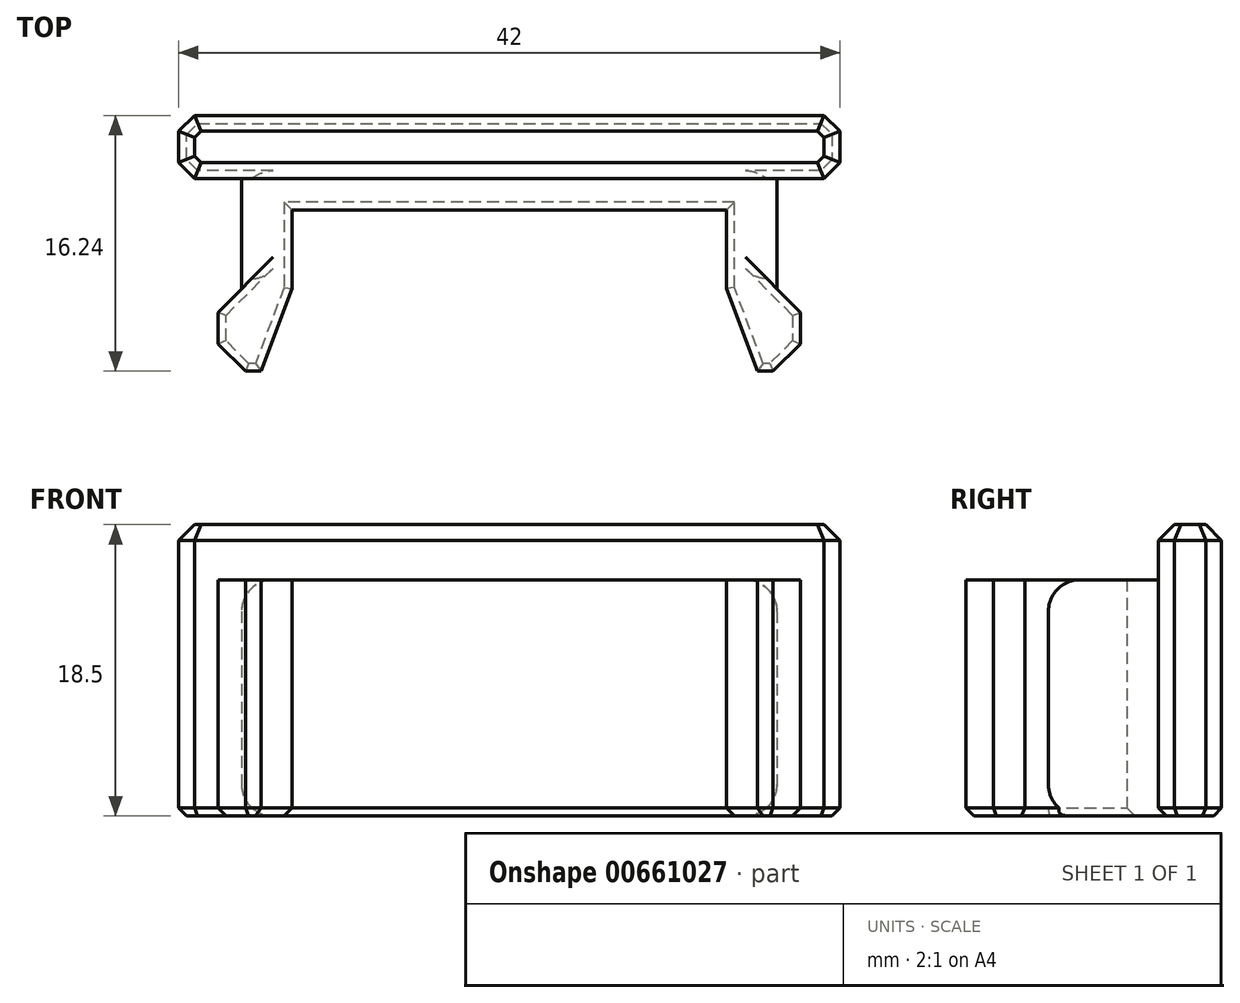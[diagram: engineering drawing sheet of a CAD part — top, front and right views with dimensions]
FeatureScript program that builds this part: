
annotation { "Feature Type Name" : "Feature", "Feature Type Description" : "" }
export const myFeature = defineFeature(function(context is Context, id is Id, definition is map)
    precondition{}
    {
        {
            var Q0;
            Q0=qCreatedBy(makeId("Top.planeOp"),FACE);
            var sketch = newSketch(context, id + "F0", { "sketchPlane" : qUnion([Q0])});
            skLineSegment(sketch, "E0.bottom", {"start": v(-20, 0) * mm, "end": v(-17.5, 0) * mm});
            skLineSegment(sketch, "E0.top", {"start": v(-20, -10) * mm, "end": v(-17.5, -10) * mm});
            skLineSegment(sketch, "E0.left", {"start": v(-20, 0) * mm, "end": v(-20, -10) * mm});
            skLineSegment(sketch, "E0.right", {"start": v(-17.5, 0) * mm, "end": v(-17.5, -10) * mm});
            skLineSegment(sketch, "E1.bottom", {"start": v(17.5, 0) * mm, "end": v(20, 0) * mm});
            skLineSegment(sketch, "E1.top", {"start": v(17.5, -10) * mm, "end": v(20, -10) * mm});
            skLineSegment(sketch, "E1.left", {"start": v(17.5, 0) * mm, "end": v(17.5, -10) * mm});
            skLineSegment(sketch, "E1.right", {"start": v(20, 0) * mm, "end": v(20, -10) * mm});
            skLineSegment(sketch, "E2", {"start": v(-20, 0) * mm, "end": v(-21, 1) * mm});
            skLineSegment(sketch, "E3", {"start": v(-21, 1) * mm, "end": v(-21, 3) * mm});
            skLineSegment(sketch, "E4", {"start": v(-21, 3) * mm, "end": v(-20, 4) * mm});
            skLineSegment(sketch, "E5", {"start": v(-20, 4) * mm, "end": v(0, 4) * mm});
            skLineSegment(sketch, "E6", {"start": v(-17.5, 0) * mm, "end": v(-17, 0) * mm});
            skLineSegment(sketch, "E7", {"start": v(-17, 0) * mm, "end": v(-17, -7) * mm});
            skLineSegment(sketch, "E8", {"start": v(-17, -7) * mm, "end": v(-18.5, -8.5) * mm});
            skLineSegment(sketch, "E9", {"start": v(-18.5, -8.5) * mm, "end": v(-18.5, -10.5) * mm});
            skLineSegment(sketch, "E10", {"start": v(-18.5, -10.5) * mm, "end": v(-16.76, -12.24) * mm});
            skLineSegment(sketch, "E11", {"start": v(-16.76, -12.24) * mm, "end": v(-15.76, -12.24) * mm});
            skLineSegment(sketch, "E12", {"start": v(-15.76, -12.24) * mm, "end": v(-13.8, -7) * mm});
            skLineSegment(sketch, "E13", {"start": v(-13.8, -7) * mm, "end": v(-13.8, -2) * mm});
            skLineSegment(sketch, "E14", {"start": v(-13.8, -2) * mm, "end": v(0, -2) * mm});
            skLineSegment(sketch, "E15.MirrorCS", {"start": v(20, 4) * mm, "end": v(0, 4) * mm});
            skLineSegment(sketch, "E16.MirrorCS", {"start": v(21, 3) * mm, "end": v(20, 4) * mm});
            skLineSegment(sketch, "E17.MirrorCS", {"start": v(21, 1) * mm, "end": v(21, 3) * mm});
            skLineSegment(sketch, "E18.MirrorCS", {"start": v(20, 0) * mm, "end": v(21, 1) * mm});
            skLineSegment(sketch, "E19.MirrorCS", {"start": v(17.5, 0) * mm, "end": v(17, 0) * mm});
            skLineSegment(sketch, "E20.MirrorCS", {"start": v(17, 0) * mm, "end": v(17, -7) * mm});
            skLineSegment(sketch, "E21.MirrorCS", {"start": v(17, -7) * mm, "end": v(18.5, -8.5) * mm});
            skLineSegment(sketch, "E22.MirrorCS", {"start": v(18.5, -8.5) * mm, "end": v(18.5, -10.5) * mm});
            skLineSegment(sketch, "E23.MirrorCS", {"start": v(18.5, -10.5) * mm, "end": v(16.76, -12.24) * mm});
            skLineSegment(sketch, "E24.MirrorCS", {"start": v(16.76, -12.24) * mm, "end": v(15.76, -12.24) * mm});
            skLineSegment(sketch, "E25.MirrorCS", {"start": v(15.76, -12.24) * mm, "end": v(13.8, -7) * mm});
            skLineSegment(sketch, "E26.MirrorCS", {"start": v(13.8, -7) * mm, "end": v(13.8, -2) * mm});
            skLineSegment(sketch, "E27.MirrorCS", {"start": v(13.8, -2) * mm, "end": v(0, -2) * mm});
            skSolve(sketch);
        }
        {
            var Q0;
            Q0=makeQuery(id+"F0.imprint","IMPRINT",FACE,{"disambiguationData":[TD([[makeQuery(id+"F0.imprint","IMPRINT",EDGE,{"derivedFrom":sQuery(id+"F0.wireOp",EDGE,"E0.bottom")}),1.0]])]});
            var Q1;
            {var subQ0=sQuery(id+"F0.wireOp",EDGE,"E0.right");var subQ1=sQuery(id+"F0.wireOp",EDGE,"E0.top");var subQ2=makeQuery(id+"F0.imprint","INTERSECT",VERTEX,{"derivedFrom":[subQ1,subQ0]});Q1=makeQuery(id+"F0.imprint","IMPRINT",FACE,{"disambiguationData":[TD([[makeQuery(id+"F0.imprint","IMPRINT",EDGE,{"disambiguationData":[TD([[subQ2,1.0]])],"derivedFrom":subQ1}),1.0]])]});}
            var Q2;
            {var subQ0=sQuery(id+"F0.wireOp",EDGE,"E1.left");var subQ1=sQuery(id+"F0.wireOp",EDGE,"E1.top");var subQ2=makeQuery(id+"F0.imprint","INTERSECT",VERTEX,{"derivedFrom":[subQ1,subQ0]});Q2=makeQuery(id+"F0.imprint","IMPRINT",FACE,{"disambiguationData":[TD([[makeQuery(id+"F0.imprint","IMPRINT",EDGE,{"disambiguationData":[TD([[subQ2,-1.0]])],"derivedFrom":subQ1}),1.0]])]});}
            extrude(context, id + "F1", {"entities" : qUnion([Q0, Q1, Q2]), "depth" : 15 * mm, "offsetDistance" : 25 * mm});
        }
        {
            var Q0;
            Q0=makeQuery(id+"F1.opExtrude","CAP_FACE",FACE,{"disambiguationData":[OSD([sQuery(id+"F0.wireOp",EDGE,"E0.bottom"),sQuery(id+"F0.wireOp",EDGE,"E1.bottom"),sQuery(id+"F0.wireOp",EDGE,"E2"),sQuery(id+"F0.wireOp",EDGE,"E3"),sQuery(id+"F0.wireOp",EDGE,"E4"),sQuery(id+"F0.wireOp",EDGE,"E5"),sQuery(id+"F0.wireOp",EDGE,"E6"),sQuery(id+"F0.wireOp",EDGE,"E7"),sQuery(id+"F0.wireOp",EDGE,"E8"),sQuery(id+"F0.wireOp",EDGE,"E9"),sQuery(id+"F0.wireOp",EDGE,"E10"),sQuery(id+"F0.wireOp",EDGE,"E11"),sQuery(id+"F0.wireOp",EDGE,"E12"),sQuery(id+"F0.wireOp",EDGE,"E13"),sQuery(id+"F0.wireOp",EDGE,"E14"),sQuery(id+"F0.wireOp",EDGE,"E15.MirrorCS"),sQuery(id+"F0.wireOp",EDGE,"E16.MirrorCS"),sQuery(id+"F0.wireOp",EDGE,"E17.MirrorCS"),sQuery(id+"F0.wireOp",EDGE,"E18.MirrorCS"),sQuery(id+"F0.wireOp",EDGE,"E19.MirrorCS"),sQuery(id+"F0.wireOp",EDGE,"E20.MirrorCS"),sQuery(id+"F0.wireOp",EDGE,"E21.MirrorCS"),sQuery(id+"F0.wireOp",EDGE,"E22.MirrorCS"),sQuery(id+"F0.wireOp",EDGE,"E23.MirrorCS"),sQuery(id+"F0.wireOp",EDGE,"E24.MirrorCS"),sQuery(id+"F0.wireOp",EDGE,"E25.MirrorCS"),sQuery(id+"F0.wireOp",EDGE,"E26.MirrorCS"),sQuery(id+"F0.wireOp",EDGE,"E27.MirrorCS")])],"isStart":false});
            var sketch = newSketch(context, id + "F2", { "sketchPlane" : qUnion([Q0])});
            skLineSegment(sketch, "E28", {"start": v(-17, 0) * mm, "end": v(17, 0) * mm});
            skSolve(sketch);
        }
        {
            var Q0;
            Q0=makeQuery(id+"F2.imprint","IMPRINT",FACE,{"disambiguationData":[TD([[makeQuery(id+"F2.imprint","IMPRINT",EDGE,{"derivedFrom":sQuery(id+"F2.wireOp",EDGE,"E28")}),1.0]])]});
            extrude(context, id + "F3", {"entities" : qUnion([Q0]), "operationType" : NewBodyOperationType.ADD, "depth" : 3.5 * mm, "offsetDistance" : 25 * mm});
        }
        {
            var Q0;
            Q0=makeQuery(id+"F3.opExtrude","CAP_FACE",FACE,{"disambiguationData":[OSD([sQuery(id+"F0.wireOp",EDGE,"E0.bottom"),sQuery(id+"F0.wireOp",EDGE,"E1.bottom"),sQuery(id+"F0.wireOp",EDGE,"E2"),sQuery(id+"F0.wireOp",EDGE,"E3"),sQuery(id+"F0.wireOp",EDGE,"E4"),sQuery(id+"F0.wireOp",EDGE,"E5"),sQuery(id+"F0.wireOp",EDGE,"E6"),sQuery(id+"F0.wireOp",EDGE,"E15.MirrorCS"),sQuery(id+"F0.wireOp",EDGE,"E16.MirrorCS"),sQuery(id+"F0.wireOp",EDGE,"E17.MirrorCS"),sQuery(id+"F0.wireOp",EDGE,"E18.MirrorCS"),sQuery(id+"F0.wireOp",EDGE,"E19.MirrorCS"),sQuery(id+"F2.wireOp",EDGE,"E28")])],"isStart":false});
            chamfer(context, id + "F4", {"entities" : qUnion([Q0]), "width" : 1 * mm, "tangentPropagation" : true});
        }
        {
            var Q0;
            Q0=makeQuery(id+"F1.opExtrude","CAP_EDGE",EDGE,{"disambiguationData":[OSD([sQuery(id+"F0.wireOp",EDGE,"E7")])],"isStart":true});
            var Q1;
            Q1=makeQuery(id+"F1.opExtrude","CAP_EDGE",EDGE,{"disambiguationData":[OSD([sQuery(id+"F0.wireOp",EDGE,"E7")])],"isStart":false});
            var Q2;
            Q2=makeQuery(id+"F1.opExtrude","CAP_EDGE",EDGE,{"disambiguationData":[OSD([sQuery(id+"F0.wireOp",EDGE,"E20.MirrorCS")])],"isStart":true});
            var Q3;
            Q3=makeQuery(id+"F1.opExtrude","CAP_EDGE",EDGE,{"disambiguationData":[OSD([sQuery(id+"F0.wireOp",EDGE,"E20.MirrorCS")])],"isStart":false});
            fillet(context, id + "F5", {"entities" : qUnion([Q0, Q1, Q2, Q3]), "radius" : 2 * mm, "tangentPropagation" : true, "allowEdgeOverflow" : false});
        }
        {
            var Q0;
            Q0=makeQuery(id+"F1.opExtrude","CAP_FACE",FACE,{"disambiguationData":[OSD([sQuery(id+"F0.wireOp",EDGE,"E0.bottom"),sQuery(id+"F0.wireOp",EDGE,"E1.bottom"),sQuery(id+"F0.wireOp",EDGE,"E2"),sQuery(id+"F0.wireOp",EDGE,"E3"),sQuery(id+"F0.wireOp",EDGE,"E4"),sQuery(id+"F0.wireOp",EDGE,"E5"),sQuery(id+"F0.wireOp",EDGE,"E6"),sQuery(id+"F0.wireOp",EDGE,"E7"),sQuery(id+"F0.wireOp",EDGE,"E8"),sQuery(id+"F0.wireOp",EDGE,"E9"),sQuery(id+"F0.wireOp",EDGE,"E10"),sQuery(id+"F0.wireOp",EDGE,"E11"),sQuery(id+"F0.wireOp",EDGE,"E12"),sQuery(id+"F0.wireOp",EDGE,"E13"),sQuery(id+"F0.wireOp",EDGE,"E14"),sQuery(id+"F0.wireOp",EDGE,"E15.MirrorCS"),sQuery(id+"F0.wireOp",EDGE,"E16.MirrorCS"),sQuery(id+"F0.wireOp",EDGE,"E17.MirrorCS"),sQuery(id+"F0.wireOp",EDGE,"E18.MirrorCS"),sQuery(id+"F0.wireOp",EDGE,"E19.MirrorCS"),sQuery(id+"F0.wireOp",EDGE,"E20.MirrorCS"),sQuery(id+"F0.wireOp",EDGE,"E21.MirrorCS"),sQuery(id+"F0.wireOp",EDGE,"E22.MirrorCS"),sQuery(id+"F0.wireOp",EDGE,"E23.MirrorCS"),sQuery(id+"F0.wireOp",EDGE,"E24.MirrorCS"),sQuery(id+"F0.wireOp",EDGE,"E25.MirrorCS"),sQuery(id+"F0.wireOp",EDGE,"E26.MirrorCS"),sQuery(id+"F0.wireOp",EDGE,"E27.MirrorCS")])],"isStart":true});
            chamfer(context, id + "F6", {"entities" : qUnion([Q0]), "width" : .5 * mm, "tangentPropagation" : true});
        }
    });
